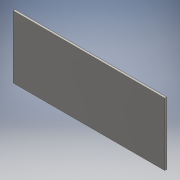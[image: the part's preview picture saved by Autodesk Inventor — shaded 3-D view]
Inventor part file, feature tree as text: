
AUTODESK INVENTOR PART (.ipt)
format: ipt  version: 2016 (Build 200138000, 138)  size: 102,400 bytes
history: native  units: mm
features: extrude x1, sketch x1
ambient origin geometry x8: Origin, YZ Plane, XZ Plane, XY Plane, X Axis, Y Axis, Z Axis, Center Point
bodies: Solid1 (feature_tree)
feature tree (2):
  extrude  "Extrusion1"  Depth=1820.0mm
  sketch  "Sketch1"  dims[d0=4406.64mm d1=1820.0mm d2=60.0mm d3=0.0mm]
